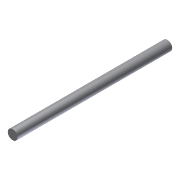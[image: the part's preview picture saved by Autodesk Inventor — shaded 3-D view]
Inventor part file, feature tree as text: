
AUTODESK INVENTOR PART (.ipt)
format: ipt  version: 2012 (Build 160160000, 160)  size: 66,048 bytes
history: native  units: in
note: dims shown in document units (in); Inventor stores cm internally (conversion verified against a paired STEP export)
features: extrude x1, sketch x1
ambient origin geometry x8: Origin, YZ Plane, XZ Plane, XY Plane, X Axis, Y Axis, Z Axis, Center Point
bodies: Solid1 (feature_tree)
feature tree (2):
  extrude  "Extrusion1"  Depth=6.0in TaperAngle=0.0deg
  sketch  "Sketch1"  dims[d0=0.375in d1=6.0in d2=0.0in]
